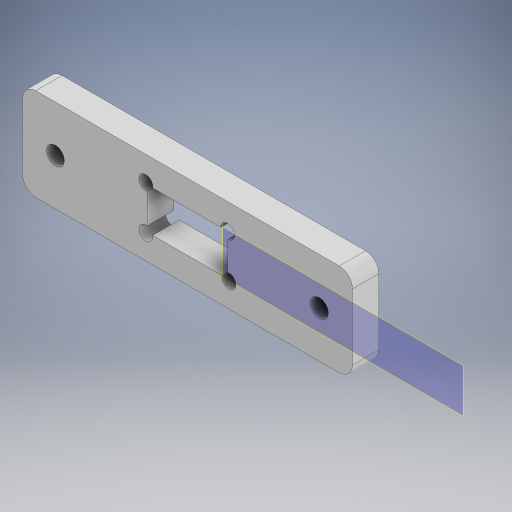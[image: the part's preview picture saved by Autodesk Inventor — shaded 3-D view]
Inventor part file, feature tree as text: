
AUTODESK INVENTOR PART (.ipt)
format: ipt  version: 2024 (Build 280153000, 153)  size: 289,792 bytes
history: native  units: mm
features: other x5, reference x3, extrude x1, fillet x1, sketch x1
ambient origin geometry x8: Origin, YZ Plane, XZ Plane, XY Plane, X Axis, Y Axis, Z Axis, Center Point
bodies: Body1 (feature_tree)
feature tree (11):
  other  "솔리드1"
  other  "작업 평면1"
  extrude  "돌출1"  Depth=0.1mm
  fillet  "모깎기1"  Radius=4.0mm
  sketch  "스케치1"
  reference  "참조1"
  reference  "참조2"
  reference  "참조3"
  other  "<userpath>\Desktop\ZIG\조립품1.iam"
  other  "조립품1.iam"
  other  "waist_64:1"
